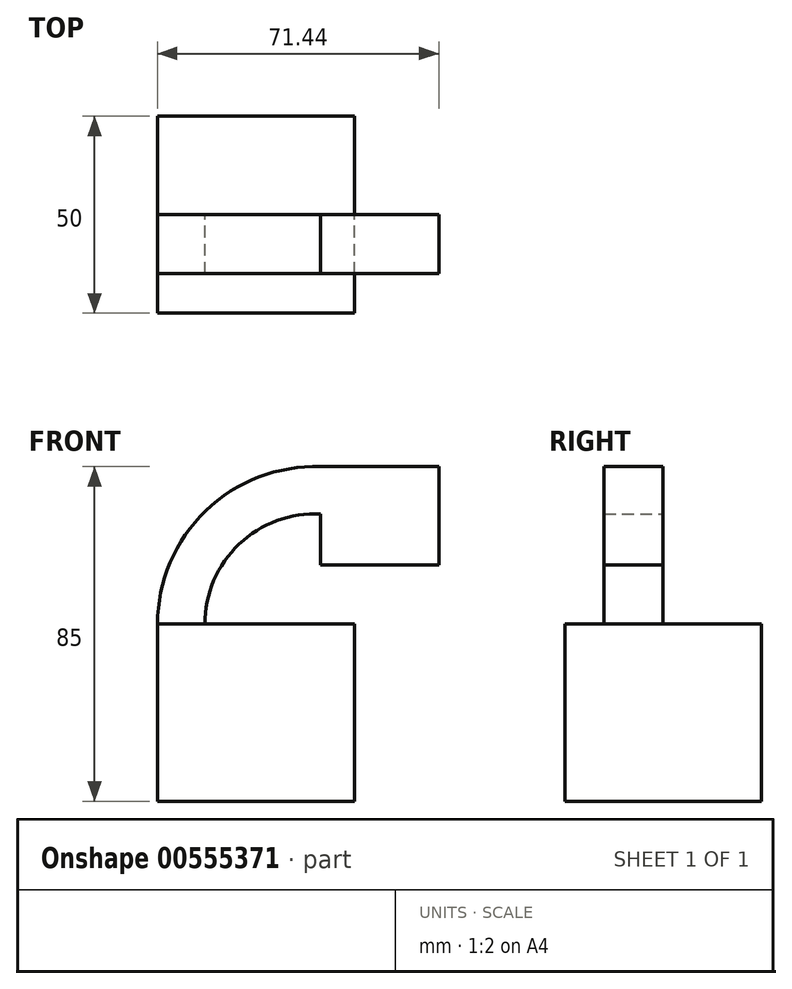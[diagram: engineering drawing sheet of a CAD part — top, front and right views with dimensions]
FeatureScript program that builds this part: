
annotation { "Feature Type Name" : "Feature", "Feature Type Description" : "" }
export const myFeature = defineFeature(function(context is Context, id is Id, definition is map)
    precondition{}
    {
        {
            var Q0;
            Q0=qCreatedBy(makeId("Front.planeOp"),FACE);
            var sketch = newSketch(context, id + "F0", { "sketchPlane" : qUnion([Q0])});
            skLineSegment(sketch, "E0.bottom", {"start": v(-25, -22.5) * mm, "end": v(25, -22.5) * mm});
            skLineSegment(sketch, "E0.top", {"start": v(-25, 22.5) * mm, "end": v(25, 22.5) * mm});
            skLineSegment(sketch, "E0.left", {"start": v(-25, -22.5) * mm, "end": v(-25, 22.5) * mm});
            skLineSegment(sketch, "E0.right", {"start": v(25, -22.5) * mm, "end": v(25, 22.5) * mm});
            skPoint(sketch, "E0.middle", {"position": v(0, 0) * mm});
            skLineSegment(sketch, "E1.bottom", {"start": v(36.44, 37.47) * mm, "end": v(16.44, 37.47) * mm});
            skLineSegment(sketch, "E1.top", {"start": v(36.44, 62.47) * mm, "end": v(16.44, 62.47) * mm});
            skLineSegment(sketch, "E1.left", {"start": v(36.44, 37.47) * mm, "end": v(36.44, 62.47) * mm});
            skLineSegment(sketch, "E1.right", {"start": v(16.44, 37.47) * mm, "end": v(16.44, 62.47) * mm});
            skPoint(sketch, "E1.middle", {"position": v(26.44, 49.97) * mm});
            skArc(sketch, "E2", {"start": v(-25, 22.5) * mm, "mid": v(-12.77, 51.3) * mm, "end": v(16.44, 62.47) * mm});
            skArc(sketch, "E3.0", {"start": v(-13, 22.5) * mm, "mid": v(-4.28, 42.8) * mm, "end": v(16.44, 50.46) * mm});
            skLineSegment(sketch, "E4", {"start": v(16.44, 50.46) * mm, "end": v(16.44, 62.47) * mm});
            skSolve(sketch);
        }
        {
            var Q0;
            Q0=makeQuery(id+"F0.imprint","IMPRINT",FACE,{"disambiguationData":[TD([[makeQuery(id+"F0.imprint","IMPRINT",EDGE,{"derivedFrom":sQuery(id+"F0.wireOp",EDGE,"E0.bottom")}),1.0]])]});
            extrude(context, id + "F1", {"entities" : qUnion([Q0]), "endBound" : BoundingType.SYMMETRIC, "depth" : 50 * mm, "offsetDistance" : 25 * mm});
        }
        {
            var Q0;
            Q0 = qSketchRegion(id + "F0", true);
            extrude(context, id + "F2", {"entities" : qUnion([Q0]), "operationType" : NewBodyOperationType.ADD, "depth" : 15 * mm, "offsetDistance" : 25 * mm});
        }
        {
            var Q0;
            Q0=makeQuery(id+"F2.opExtrude","SWEPT_FACE",FACE,{"disambiguationData":[OSD([sQuery(id+"F0.wireOp",EDGE,"E1.left")])]});
            extrude(context, id + "F3", {"entities" : qUnion([Q0]), "operationType" : NewBodyOperationType.ADD, "depth" : 10 * mm, "offsetDistance" : 25 * mm});
        }
    });
